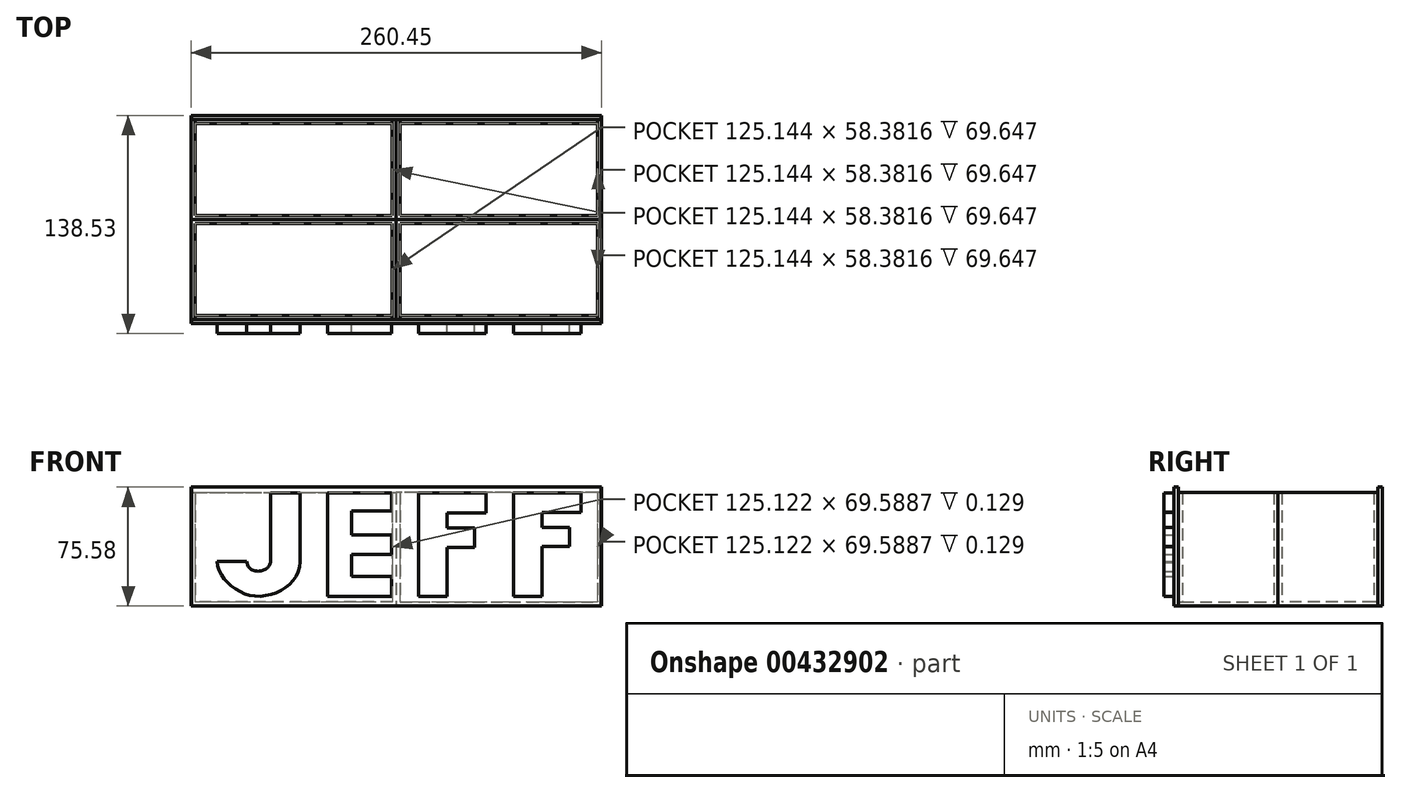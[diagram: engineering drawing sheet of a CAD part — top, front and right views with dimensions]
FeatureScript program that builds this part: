
annotation { "Feature Type Name" : "Feature", "Feature Type Description" : "" }
export const myFeature = defineFeature(function(context is Context, id is Id, definition is map)
    precondition{}
    {
        {
            var Q0;
            Q0=qCreatedBy(makeId("Front.planeOp"),FACE);
            var sketch = newSketch(context, id + "F0", { "sketchPlane" : qUnion([Q0])});
            skLineSegment(sketch, "E0", {"start": v(-57.73, 49.07) * mm, "end": v(-57.73, 6.35) * mm});
            skLineSegment(sketch, "E1", {"start": v(-72.74, 7.04) * mm, "end": v(-91.67, 7.04) * mm});
            skFitSpline(sketch, "E2", {"points": [v(-57.73, 6.35) * mm, v(-72.74, 7.04) * mm], "startDerivative": vector(-1.39, -19.05) * mm, "endDerivative": vector(-2.08, 28.4) * mm});
            skLineSegment(sketch, "E3", {"start": v(-21.47, -15.12) * mm, "end": v(19.17, -15.12) * mm});
            skLineSegment(sketch, "E4", {"start": v(19.17, -15.12) * mm, "end": v(19.17, -2.42) * mm});
            skLineSegment(sketch, "E5", {"start": v(19.17, -2.42) * mm, "end": v(-6, -2.42) * mm});
            skLineSegment(sketch, "E6", {"start": v(-6, -2.42) * mm, "end": v(-6, 11.43) * mm});
            skLineSegment(sketch, "E7", {"start": v(-6, 11.43) * mm, "end": v(19.17, 11.43) * mm});
            skLineSegment(sketch, "E8", {"start": v(19.17, 11.43) * mm, "end": v(19.17, 23.9) * mm});
            skLineSegment(sketch, "E9", {"start": v(19.17, 23.9) * mm, "end": v(-6, 23.9) * mm});
            skLineSegment(sketch, "E10", {"start": v(-6, 23.9) * mm, "end": v(-6, 39.14) * mm});
            skLineSegment(sketch, "E11", {"start": v(-6, 39.14) * mm, "end": v(19.17, 39.14) * mm});
            skLineSegment(sketch, "E12", {"start": v(19.17, 39.14) * mm, "end": v(19.17, 50.45) * mm});
            skLineSegment(sketch, "E13", {"start": v(19.17, 50.45) * mm, "end": v(-21.47, 50.45) * mm});
            skLineSegment(sketch, "E14", {"start": v(-21.47, 50.45) * mm, "end": v(-21.47, -15.12) * mm});
            skLineSegment(sketch, "E15", {"start": v(-57.73, 49.07) * mm, "end": v(-57.73, 50.45) * mm});
            skLineSegment(sketch, "E16", {"start": v(-57.73, 50.45) * mm, "end": v(-38.87, 50.45) * mm});
            skLineSegment(sketch, "E17", {"start": v(-38.87, 50.45) * mm, "end": v(-38.87, 6.52) * mm});
            skFitSpline(sketch, "E18", {"points": [v(-91.67, 7.04) * mm, v(-66, -15.12) * mm, v(-38.87, 6.52) * mm], "startDerivative": vector(6.28, -68.37) * mm, "endDerivative": vector(-1.48, 74.9) * mm});
            skLineSegment(sketch, "E19", {"start": v(36.53, -15.12) * mm, "end": v(36.53, 50.45) * mm});
            skLineSegment(sketch, "E20", {"start": v(36.53, 50.45) * mm, "end": v(79.33, 50.45) * mm});
            skLineSegment(sketch, "E21", {"start": v(79.33, 50.45) * mm, "end": v(79.33, 37.77) * mm});
            skLineSegment(sketch, "E22", {"start": v(79.33, 37.77) * mm, "end": v(54.45, 37.77) * mm});
            skLineSegment(sketch, "E23", {"start": v(54.45, 37.77) * mm, "end": v(54.45, 28.31) * mm});
            skLineSegment(sketch, "E24", {"start": v(54.45, 28.31) * mm, "end": v(71.87, 28.31) * mm});
            skLineSegment(sketch, "E25", {"start": v(71.87, 28.31) * mm, "end": v(71.87, 15.87) * mm});
            skLineSegment(sketch, "E26", {"start": v(71.87, 15.87) * mm, "end": v(54.45, 15.87) * mm});
            skLineSegment(sketch, "E27", {"start": v(54.45, 15.87) * mm, "end": v(54.45, -15.12) * mm});
            skLineSegment(sketch, "E28", {"start": v(36.53, -15.12) * mm, "end": v(54.45, -15.12) * mm});
            skLineSegment(sketch, "E29", {"start": v(96.75, 50.45) * mm, "end": v(96.75, -15.12) * mm});
            skLineSegment(sketch, "E30", {"start": v(96.75, 50.45) * mm, "end": v(139.55, 50.45) * mm});
            skLineSegment(sketch, "E31", {"start": v(139.55, 50.45) * mm, "end": v(139.55, 38.02) * mm});
            skLineSegment(sketch, "E32", {"start": v(139.55, 38.02) * mm, "end": v(114.92, 38.02) * mm});
            skLineSegment(sketch, "E33", {"start": v(114.92, 38.02) * mm, "end": v(114.92, 28.56) * mm});
            skLineSegment(sketch, "E34", {"start": v(114.92, 28.56) * mm, "end": v(132.34, 28.56) * mm});
            skLineSegment(sketch, "E35", {"start": v(132.34, 28.56) * mm, "end": v(132.34, 16.37) * mm});
            skLineSegment(sketch, "E36", {"start": v(132.34, 16.37) * mm, "end": v(114.92, 16.37) * mm});
            skLineSegment(sketch, "E37", {"start": v(114.92, 16.37) * mm, "end": v(114.92, -15.12) * mm});
            skLineSegment(sketch, "E38", {"start": v(96.75, -15.12) * mm, "end": v(114.92, -15.12) * mm});
            skSolve(sketch);
        }
        {
            var Q0;
            Q0=makeQuery(id+"F0.imprint","IMPRINT",FACE,{"disambiguationData":[TD([[makeQuery(id+"F0.imprint","IMPRINT",EDGE,{"derivedFrom":sQuery(id+"F0.wireOp",EDGE,"E0")}),1.0]])]});
            var Q1;
            Q1=makeQuery(id+"F0.imprint","IMPRINT",FACE,{"disambiguationData":[TD([[makeQuery(id+"F0.imprint","IMPRINT",EDGE,{"derivedFrom":sQuery(id+"F0.wireOp",EDGE,"E3")}),1.0]])]});
            var Q2;
            Q2=makeQuery(id+"F0.imprint","IMPRINT",FACE,{"disambiguationData":[TD([[makeQuery(id+"F0.imprint","IMPRINT",EDGE,{"derivedFrom":sQuery(id+"F0.wireOp",EDGE,"E19")}),-1.0]])]});
            var Q3;
            Q3=makeQuery(id+"F0.imprint","IMPRINT",FACE,{"disambiguationData":[TD([[makeQuery(id+"F0.imprint","IMPRINT",EDGE,{"derivedFrom":sQuery(id+"F0.wireOp",EDGE,"E29")}),1.0]])]});
            extrude(context, id + "F1", {"entities" : qUnion([Q0, Q1, Q2, Q3]), "depth" : 6.35 * mm});
        }
        {
            var Q0;
            Q0=qCreatedBy(makeId("Right.planeOp"),FACE);
            var sketch = newSketch(context, id + "F2", { "sketchPlane" : qUnion([Q0])});
            skLineSegment(sketch, "E39.bottom", {"start": v(0, 54.19) * mm, "end": v(2.67, 54.19) * mm});
            skLineSegment(sketch, "E39.top", {"start": v(0, -21.33) * mm, "end": v(2.67, -21.33) * mm});
            skLineSegment(sketch, "E39.left", {"start": v(0, 54.19) * mm, "end": v(0, -21.33) * mm});
            skLineSegment(sketch, "E39.right", {"start": v(2.67, 54.19) * mm, "end": v(2.67, -21.33) * mm});
            skSolve(sketch);
        }
        {
            var Q0;
            Q0=makeQuery(id+"F2.imprint","IMPRINT",FACE,{"disambiguationData":[TD([[makeQuery(id+"F2.imprint","IMPRINT",EDGE,{"derivedFrom":sQuery(id+"F2.wireOp",EDGE,"E39.bottom")}),-1.0]])]});
            extrude(context, id + "F3", {"entities" : qUnion([Q0]), "depth" : 152.4 * mm, "hasSecondDirection" : true, "secondDirectionOppositeDirection" : true, "secondDirectionDepth" : 107.95 * mm});
        }
        {
            var Q0;
            Q0=qCreatedBy(makeId("Top.planeOp"),FACE);
            var sketch = newSketch(context, id + "F4", { "sketchPlane" : qUnion([Q0])});
            skPoint(sketch, "E40", {"position": v(0, 2.7) * mm});
            skPoint(sketch, "E41", {"position": v(-107.97, 2.63) * mm});
            skPoint(sketch, "E42", {"position": v(152.48, 2.63) * mm});
            skLineSegment(sketch, "E43", {"start": v(-107.97, 2.63) * mm, "end": v(-107.97, 66.09) * mm});
            skLineSegment(sketch, "E44", {"start": v(-107.97, 66.09) * mm, "end": v(22.25, 66.09) * mm});
            skLineSegment(sketch, "E45", {"start": v(22.25, 66.09) * mm, "end": v(22.25, 2.63) * mm});
            skLineSegment(sketch, "E46", {"start": v(22.25, 2.63) * mm, "end": v(-107.97, 2.63) * mm});
            skSolve(sketch);
        }
        {
            var Q0;
            Q0=makeQuery(id+"F4.imprint","IMPRINT",FACE,{"disambiguationData":[TD([[makeQuery(id+"F4.imprint","IMPRINT",EDGE,{"derivedFrom":sQuery(id+"F4.wireOp",EDGE,"E43")}),-1.0]])]});
            extrude(context, id + "F5", {"entities" : qUnion([Q0]), "operationType" : NewBodyOperationType.ADD, "depth" : 50.8 * mm});
        }
        {
            var Q0;
            Q0=makeQuery(id+"F4.imprint","IMPRINT",FACE,{"disambiguationData":[TD([[makeQuery(id+"F4.imprint","IMPRINT",EDGE,{"derivedFrom":sQuery(id+"F4.wireOp",EDGE,"E43")}),-1.0]])]});
            extrude(context, id + "F6", {"entities" : qUnion([Q0]), "operationType" : NewBodyOperationType.ADD, "oppositeDirection" : true, "depth" : 21.4 * mm});
        }
        {
            var Q0;
            Q0=makeQuery(id+"F5.opExtrude","CAP_FACE",FACE,{"disambiguationData":[OSD([sQuery(id+"F4.wireOp",EDGE,"E43"),sQuery(id+"F4.wireOp",EDGE,"E44"),sQuery(id+"F4.wireOp",EDGE,"E45"),sQuery(id+"F4.wireOp",EDGE,"E46")])],"isStart":false});
            shell(context, id + "F7", {"entities" : qUnion([Q0]), "thickness" : 2.54 * mm});
        }
        {
            var Q0;
            Q0=makeQuery(id+"F3.opExtrude","SWEPT_BODY",BODY,{"disambiguationData":[OSD([sQuery(id+"F2.wireOp",EDGE,"E39.bottom"),sQuery(id+"F2.wireOp",EDGE,"E39.top"),sQuery(id+"F2.wireOp",EDGE,"E39.left"),sQuery(id+"F2.wireOp",EDGE,"E39.right")])]});
            var Q1;
            {var subQ0=sQuery(id+"F4.wireOp",EDGE,"E45");Q1=makeQuery(id+"F6.boolean.opBoolean","MERGE",FACE,{"derivedFrom":[makeQuery(id+"F5.opExtrude","SWEPT_FACE",FACE,{"disambiguationData":[OSD([subQ0])]}),makeQuery(id+"F6.opExtrude","SWEPT_FACE",FACE,{"disambiguationData":[OSD([subQ0])]})]});}
            mirror(context, id + "F8", {"entities" : qUnion([Q0]), "mirrorPlane" : qUnion([Q1])});
        }
        {
            var Q0;
            Q0=makeQuery(id+"F8.opPattern","COPY",BODY,{"derivedFrom":makeQuery(id+"F3.opExtrude","SWEPT_BODY",BODY,{"disambiguationData":[OSD([sQuery(id+"F2.wireOp",EDGE,"E39.bottom"),sQuery(id+"F2.wireOp",EDGE,"E39.top"),sQuery(id+"F2.wireOp",EDGE,"E39.left"),sQuery(id+"F2.wireOp",EDGE,"E39.right")])]}),"instanceName":"1"});
            var Q1;
            Q1=makeQuery(id+"F3.opExtrude","SWEPT_BODY",BODY,{"disambiguationData":[OSD([sQuery(id+"F2.wireOp",EDGE,"E39.bottom"),sQuery(id+"F2.wireOp",EDGE,"E39.top"),sQuery(id+"F2.wireOp",EDGE,"E39.left"),sQuery(id+"F2.wireOp",EDGE,"E39.right")])]});
            var Q2;
            {var subQ0=sQuery(id+"F4.wireOp",EDGE,"E44");Q2=makeQuery(id+"F8.opPattern","COPY",FACE,{"derivedFrom":makeQuery(id+"F6.boolean.opBoolean","MERGE",FACE,{"derivedFrom":[makeQuery(id+"F5.opExtrude","SWEPT_FACE",FACE,{"disambiguationData":[OSD([subQ0])]}),makeQuery(id+"F6.opExtrude","SWEPT_FACE",FACE,{"disambiguationData":[OSD([subQ0])]})]}),"instanceName":"1"});}
            mirror(context, id + "F9", {"entities" : qUnion([Q0, Q1]), "mirrorPlane" : qUnion([Q2])});
        }
    });
